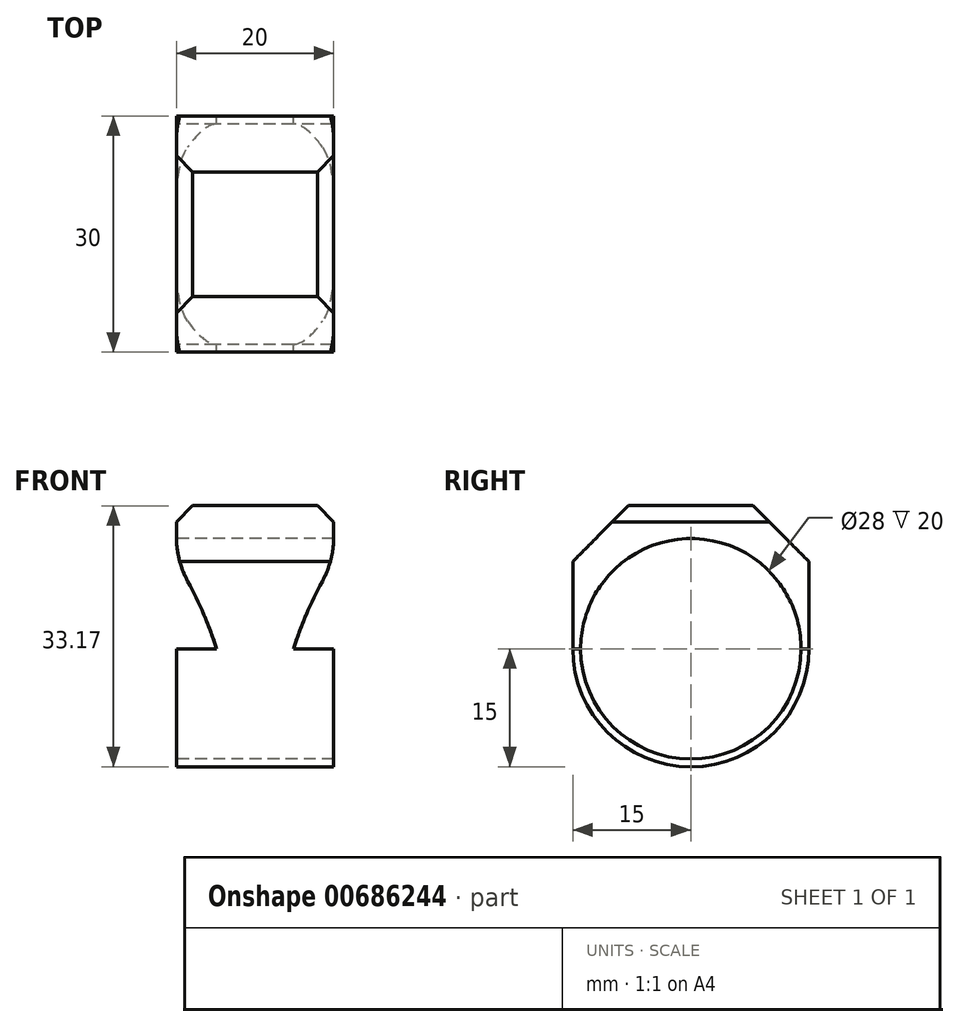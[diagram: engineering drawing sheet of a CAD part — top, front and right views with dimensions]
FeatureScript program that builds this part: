
annotation { "Feature Type Name" : "Feature", "Feature Type Description" : "" }
export const myFeature = defineFeature(function(context is Context, id is Id, definition is map)
    precondition{}
    {
        {
            var Q0;
            Q0=qCreatedBy(makeId("Right.planeOp"),FACE);
            var sketch = newSketch(context, id + "F0", { "sketchPlane" : qUnion([Q0])});
            skCircle(sketch, "E0", {"center": v(0, 0) * mm, "radius": 14 * mm});
            skArc(sketch, "E1", {"start": v(-15, 0) * mm, "mid": v(0, -15) * mm, "end": v(15, 0) * mm});
            skLineSegment(sketch, "E2", {"start": v(15, 0) * mm, "end": v(15, 21.08) * mm});
            skLineSegment(sketch, "E3", {"start": v(-15, 0) * mm, "end": v(-15, 21.08) * mm});
            skLineSegment(sketch, "E4", {"start": v(-15, 21.08) * mm, "end": v(15, 21.08) * mm});
            skSolve(sketch);
        }
        {
            var Q0;
            Q0=qSketchRegion(id+"F0",true);
            extrude(context, id + "F1", {"entities" : qUnion([Q0]), "depth" : 20 * mm, "offsetDistance" : 25 * mm});
        }
        {
            var Q0;
            Q0=makeQuery(id+"F1.opExtrude","SWEPT_EDGE",EDGE,{"disambiguationData":[OSD([sQuery(id+"F0.wireOp",EDGE,"E3"),sQuery(id+"F0.wireOp",EDGE,"E4")])]});
            var Q1;
            Q1=makeQuery(id+"F1.opExtrude","SWEPT_EDGE",EDGE,{"disambiguationData":[OSD([sQuery(id+"F0.wireOp",EDGE,"E2"),sQuery(id+"F0.wireOp",EDGE,"E4")])]});
            chamfer(context, id + "F2", {"entities" : qUnion([Q0, Q1]), "width" : 10 * mm, "tangentPropagation" : true});
        }
        {
            var Q0;
            Q0=makeQuery(id+"F1.opExtrude","SWEPT_FACE",FACE,{"disambiguationData":[OSD([sQuery(id+"F0.wireOp",EDGE,"E2")])]});
            var sketch = newSketch(context, id + "F3", { "sketchPlane" : qUnion([Q0])});
            skLineSegment(sketch, "E5", {"start": v(0, -15) * mm, "end": v(-20, -15) * mm});
            skLineSegment(sketch, "E6", {"start": v(-12.5, -15) * mm, "end": v(-7.5, -15) * mm});
            skArc(sketch, "E7", {"start": v(0, 11.08) * mm, "mid": v(-5.55, -1.44) * mm, "end": v(-7.5, -15) * mm});
            skArc(sketch, "E8", {"start": v(-12.5, -15) * mm, "mid": v(-14.45, -1.44) * mm, "end": v(-20, 11.08) * mm});
            skLineSegment(sketch, "E9", {"start": v(0, 11.08) * mm, "end": v(0, -15) * mm});
            skLineSegment(sketch, "E10", {"start": v(0, -15) * mm, "end": v(-7.5, -15) * mm});
            skLineSegment(sketch, "E11", {"start": v(-20, -15) * mm, "end": v(-20, -15) * mm});
            skLineSegment(sketch, "E12", {"start": v(-20, 11.08) * mm, "end": v(-20, -15) * mm});
            skLineSegment(sketch, "E13.trimOffspring", {"start": v(-12.5, -15) * mm, "end": v(-20, -15) * mm});
            skSolve(sketch);
        }
        {
            var Q0;
            {var subQ0=sQuery(id+"F3.wireOp",EDGE,"E9");var subQ2=sQuery(id+"F0.wireOp",EDGE,"E2");var subQ4=makeQuery(id+"F1.opExtrude","SWEPT_EDGE",EDGE,{"disambiguationData":[OSD([sQuery(id+"F0.wireOp",EDGE,"E1"),subQ2])]});var subQ6=makeQuery(id+"F3.imprint","INTERSECT",VERTEX,{"derivedFrom":[subQ4,subQ0]});Q0=makeQuery(id+"F3.imprint","IMPRINT",FACE,{"disambiguationData":[TD([[makeQuery(id+"F3.imprint","IMPRINT",EDGE,{"disambiguationData":[TD([[subQ6,1.0]])],"derivedFrom":subQ4}),1.0]])]});}
            var Q1;
            {var subQ0=sQuery(id+"F3.wireOp",EDGE,"E12");var subQ2=sQuery(id+"F0.wireOp",EDGE,"E2");var subQ4=makeQuery(id+"F1.opExtrude","SWEPT_EDGE",EDGE,{"disambiguationData":[OSD([sQuery(id+"F0.wireOp",EDGE,"E1"),subQ2])]});var subQ6=makeQuery(id+"F3.imprint","INTERSECT",VERTEX,{"derivedFrom":[subQ4,subQ0]});Q1=makeQuery(id+"F3.imprint","IMPRINT",FACE,{"disambiguationData":[TD([[makeQuery(id+"F3.imprint","IMPRINT",EDGE,{"disambiguationData":[TD([[subQ6,-1.0]])],"derivedFrom":subQ4}),1.0]])]});}
            var Q2;
            {var subQ0=sQuery(id+"F3.wireOp",EDGE,"E13.trimOffspring");Q2=makeQuery(id+"F3.imprint","IMPRINT",FACE,{"disambiguationData":[TD([[makeQuery(id+"F3.imprint","IMPRINT",EDGE,{"derivedFrom":subQ0}),-1.0]])]});}
            var Q3;
            {var subQ0=sQuery(id+"F3.wireOp",EDGE,"E10");Q3=makeQuery(id+"F3.imprint","IMPRINT",FACE,{"disambiguationData":[TD([[makeQuery(id+"F3.imprint","IMPRINT",EDGE,{"derivedFrom":subQ0}),-1.0]])]});}
            extrude(context, id + "F4", {"entities" : qUnion([Q0, Q1, Q2, Q3]), "operationType" : NewBodyOperationType.REMOVE, "oppositeDirection" : true, "depth" : 38.66 * mm, "offsetDistance" : 25 * mm});
        }
        {
            var Q0;
            {var subQ0=sQuery(id+"F0.wireOp",EDGE,"E4");var subQ1=sQuery(id+"F0.wireOp",EDGE,"E2");var subQ3=sQuery(id+"F3.wireOp",EDGE,"E8");Q0=makeQuery(id+"F4.boolean.opBoolean","COPY",EDGE,{"disambiguationData":[TD([makeQuery(id+"F1.opExtrude","SWEPT_FACE",FACE,{"disambiguationData":[OSD([subQ1])]})])],"derivedFrom":makeQuery(id+"F4.opExtrude","SWEPT_EDGE",EDGE,{"disambiguationData":[OSD([subQ1,subQ0,subQ3,sQuery(id+"F3.wireOp",EDGE,"E12")])]})});}
            var Q1;
            {var subQ0=sQuery(id+"F0.wireOp",EDGE,"E4");var subQ1=sQuery(id+"F0.wireOp",EDGE,"E3");var subQ2=sQuery(id+"F0.wireOp",EDGE,"E2");var subQ4=sQuery(id+"F3.wireOp",EDGE,"E8");Q1=makeQuery(id+"F4.boolean.opBoolean","COPY",EDGE,{"disambiguationData":[TD([makeQuery(id+"F1.opExtrude","SWEPT_FACE",FACE,{"disambiguationData":[OSD([subQ1])]})])],"derivedFrom":makeQuery(id+"F4.opExtrude","SWEPT_EDGE",EDGE,{"disambiguationData":[OSD([subQ2,subQ0,subQ4,sQuery(id+"F3.wireOp",EDGE,"E12")])]})});}
            var Q2;
            {var subQ0=sQuery(id+"F0.wireOp",EDGE,"E4");var subQ1=sQuery(id+"F0.wireOp",EDGE,"E3");var subQ2=sQuery(id+"F3.wireOp",EDGE,"E7");var subQ3=sQuery(id+"F0.wireOp",EDGE,"E2");Q2=makeQuery(id+"F4.boolean.opBoolean","COPY",EDGE,{"disambiguationData":[TD([makeQuery(id+"F1.opExtrude","SWEPT_FACE",FACE,{"disambiguationData":[OSD([subQ1])]})])],"derivedFrom":makeQuery(id+"F4.opExtrude","SWEPT_EDGE",EDGE,{"disambiguationData":[OSD([subQ3,subQ0,subQ2,sQuery(id+"F3.wireOp",EDGE,"E9")])]})});}
            var Q3;
            {var subQ0=sQuery(id+"F0.wireOp",EDGE,"E2");var subQ1=sQuery(id+"F0.wireOp",EDGE,"E4");var subQ3=sQuery(id+"F3.wireOp",EDGE,"E7");Q3=makeQuery(id+"F4.boolean.opBoolean","COPY",EDGE,{"disambiguationData":[TD([makeQuery(id+"F1.opExtrude","SWEPT_FACE",FACE,{"disambiguationData":[OSD([subQ0])]})])],"derivedFrom":makeQuery(id+"F4.opExtrude","SWEPT_EDGE",EDGE,{"disambiguationData":[OSD([subQ0,subQ1,subQ3,sQuery(id+"F3.wireOp",EDGE,"E9")])]})});}
            fillet(context, id + "F5", {"entities" : qUnion([Q0, Q1, Q2, Q3]), "radius" : 12 * mm, "tangentPropagation" : true, "allowEdgeOverflow" : false});
        }
        {
            var Q0;
            Q0=makeQuery(id+"F1.opExtrude","CAP_EDGE",EDGE,{"disambiguationData":[OSD([sQuery(id+"F0.wireOp",EDGE,"E4")])],"isStart":true});
            var Q1;
            Q1=makeQuery(id+"F1.opExtrude","CAP_EDGE",EDGE,{"disambiguationData":[OSD([sQuery(id+"F0.wireOp",EDGE,"E4")])],"isStart":false});
            chamfer(context, id + "F6", {"entities" : qUnion([Q0, Q1]), "width" : 5 * mm, "tangentPropagation" : true});
        }
        {
            var Q0;
            Q0=qCreatedBy(makeId("Right.planeOp"),FACE);
            var sketch = newSketch(context, id + "F7", { "sketchPlane" : qUnion([Q0])});
            skLineSegment(sketch, "E14.bottom", {"start": v(23.02, 60.04) * mm, "end": v(-26.86, 60.04) * mm});
            skLineSegment(sketch, "E14.top", {"start": v(23.02, 19.02) * mm, "end": v(-26.86, 19.02) * mm});
            skLineSegment(sketch, "E14.left", {"start": v(23.02, 60.04) * mm, "end": v(23.02, 19.02) * mm});
            skLineSegment(sketch, "E14.right", {"start": v(-26.86, 60.04) * mm, "end": v(-26.86, 19.02) * mm});
            skSolve(sketch);
        }
        {
            var Q0;
            Q0=qSketchRegion(id+"F7",true);
            extrude(context, id + "F8", {"entities" : qUnion([Q0]), "operationType" : NewBodyOperationType.REMOVE, "endBound" : BoundingType.SYMMETRIC, "oppositeDirection" : true, "depth" : 77.2 * mm, "offsetDistance" : 25 * mm});
        }
        {
            var Q0;
            Q0=qCreatedBy(makeId("Right.planeOp"),FACE);
            var sketch = newSketch(context, id + "F9", { "sketchPlane" : qUnion([Q0])});
            skLineSegment(sketch, "E15.bottom", {"start": v(-13.69, 28.17) * mm, "end": v(13.45, 28.17) * mm});
            skLineSegment(sketch, "E15.top", {"start": v(-13.69, 18.17) * mm, "end": v(13.45, 18.17) * mm});
            skLineSegment(sketch, "E15.left", {"start": v(-13.69, 28.17) * mm, "end": v(-13.69, 18.17) * mm});
            skLineSegment(sketch, "E15.right", {"start": v(13.45, 28.17) * mm, "end": v(13.45, 18.17) * mm});
            skSolve(sketch);
        }
        {
            var Q0;
            Q0=makeQuery(id+"F9.imprint","IMPRINT",FACE,{"disambiguationData":[TD([[makeQuery(id+"F9.imprint","IMPRINT",EDGE,{"derivedFrom":sQuery(id+"F9.wireOp",EDGE,"E15.bottom")}),-1.0]])]});
            extrude(context, id + "F10", {"entities" : qUnion([Q0]), "operationType" : NewBodyOperationType.REMOVE, "depth" : 50.5 * mm, "offsetDistance" : 25 * mm});
        }
    });
